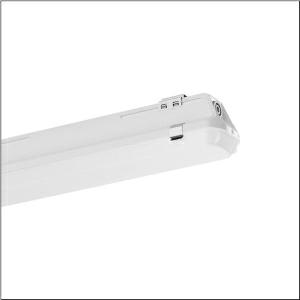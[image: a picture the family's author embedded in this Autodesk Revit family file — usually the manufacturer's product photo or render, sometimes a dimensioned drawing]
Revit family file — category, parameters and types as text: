
# Revit family: monsun_r__21_51fb10dp440b_4f1d
name_source: partatom
category: Lighting Fixtures
units: mm (PartAtom-declared; Revit-internal decimal feet)

## family parameters
Cut with Voids When Loaded = No
Host = Face
Light Source = No
Part Type = Normal
Room Calculation Point = No
Round Connector Dimension = Use Diameter
Shared = No

## types (1)
- --- (1 x LED, 4360 lm, 27.9 W, 4000K)
    Apparent Load = 28 VA
    CIE Flux Codes = 47 77 93 94 100
    Color Rendering = 80
    Color Temperature = 4000K
    Default Elevation = 1800 mm
    Description = Monsun® 21, damp-proof luminaire, chain hanger, primary optical cover: enclosure, of PMMA, light emission: direct distribution, primary light characteristic: symmetric, installation type: suspended mounting, surface-mounted, horizontal mounting, vertical mounting, LED, rated luminous flux: 4.360lm, luminous efficacy: 156lm/W, light colour: 840, colour temperature: 4000K, control gear: ECG DALI, with terminal, 5-pole, max. 2.5mm², mains connection: 220..240V, AC, 50/60Hz, rated input power: 28W, housing, of glass-fibre reinforced polyester, uncoated, bright grey, incl. chain hanger, length: 1.590mm, width: 90mm, height: 88mm, clip for enclosure, of stainless steel (V2A), ceiling mounting element, of stainless steel (V2A), chain hanger, of stainless steel (V2A), protection rating (complete): IP66, insulation class (complete): insulation class I (protective earthing), certification: CE, ENEC, VDE, UKCA, protection symbol: D, impact resistance: IK04, permissible operating ambient temperature: -25..+35°C, standard: EN 50419, EN 60598-2-1, corresponds to IFS (International Featured Standards) requirements for safety and quality in the food industry, for indoor or canopied outdoor use, no direct snow, no direct sun, no direct rain, contact your sales advisor before using the luminaires in applications with unclear chemical exposure, large temperature fluctuations or condensation-forming humidity, LABS conformity tested according to VDMA 24364:2018-05, packaging unit: 1 piece
    Height = 89 mm
    Lamp = 1 x LED
    Lamp Light Flux = 4360 lm
    Lamp Power = 27.9 W
    Lamp count = 1
    Length = 1590 mm
    Luminous efficacy = 156 lm/W
    Manufacturer = Siteco
    ModVariant = No
    Model = 51FB10DP440B
    Mounting Place = Ceiling
    Mounting Type = Surface mounted
    Number of Poles = 1
    OnlyDefault = Yes
    Power Factor = 1
    Product Name = Monsun® 21
    Product group = damp-proof luminaire
    ProductGroupID = 301
    Protection Class = Protection class I
    Protection Degree = IP 66
    RLX_Detail_Level = 1
    RLX_Emergency_Light_Flux = 0 lm
    RLX_Emergency_Type = 0
    RLX_Emergency_Type_DB = No
    RlxData = <blob elided: 92169 chars, md5=9b300ca8>
    Socket = socket
    Standby Power = 0 W
    System Light Flux = 4360 lm
    System Power = 28 W
    Type Comments = factory setting: luminous flux: 100 % | dim-lin: 254 | 184 mA
    Type Image = l_1006717.jpg
    URL = http://relux.com
    VarID = @adj_152463
    Voltage = 0 V
    Weight = 0.00 kg
    Width = 90 mm

## geometry (parser evidence)
native form markers: Blend x4, Sweep x12
no freeform markers — native parametric forms only
